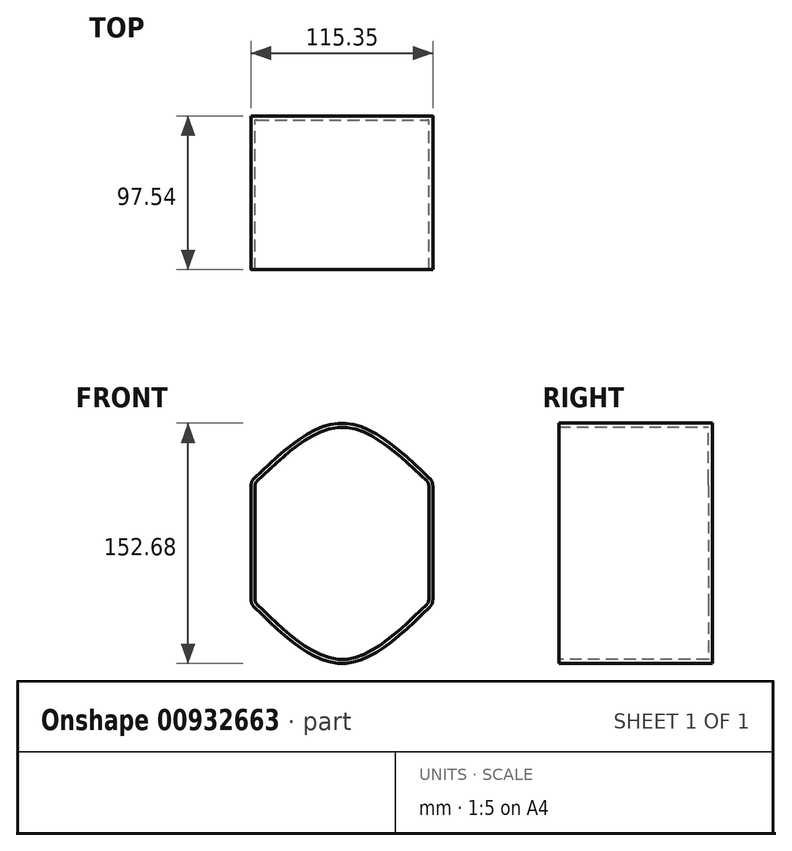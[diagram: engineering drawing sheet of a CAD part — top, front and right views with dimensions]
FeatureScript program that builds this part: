
annotation { "Feature Type Name" : "Feature", "Feature Type Description" : "" }
export const myFeature = defineFeature(function(context is Context, id is Id, definition is map)
    precondition{}
    {
        {
            var Q0;
            Q0=qCreatedBy(makeId("Front.planeOp"),FACE);
            var sketch = newSketch(context, id + "F0", { "sketchPlane" : qUnion([Q0])});
            skLineSegment(sketch, "E0.left", {"start": v(-56.92, 36.54) * mm, "end": v(-56.92, -36.1) * mm});
            skLineSegment(sketch, "E0.right", {"start": v(58.43, 36.54) * mm, "end": v(58.43, -36.1) * mm});
            skFitSpline(sketch, "E1", {"points": [v(-56.92, 39.25) * mm, v(0.75, 76.2) * mm, v(58.43, 39.25) * mm], "startDerivative": vector(115.35, 110.85) * mm, "endDerivative": vector(115.35, -110.85) * mm});
            skFitSpline(sketch, "E2", {"points": [v(-56.92, -38.77) * mm, v(0.75, -76.48) * mm, v(58.43, -38.77) * mm], "startDerivative": vector(115.35, -113.14) * mm, "endDerivative": vector(115.35, 113.14) * mm});
            skArc(sketch, "E3.filletArc", {"start": v(-54.97, 41.12) * mm, "mid": v(-56.41, 39.03) * mm, "end": v(-56.92, 36.54) * mm});
            skArc(sketch, "E4.filletArc", {"start": v(-56.92, -36.1) * mm, "mid": v(-56.43, -38.56) * mm, "end": v(-55.02, -40.63) * mm});
            skArc(sketch, "E5.filletArc", {"start": v(56.52, -40.63) * mm, "mid": v(57.93, -38.56) * mm, "end": v(58.43, -36.1) * mm});
            skArc(sketch, "E6.filletArc", {"start": v(58.43, 36.54) * mm, "mid": v(57.92, 39.03) * mm, "end": v(56.48, 41.12) * mm});
            skSolve(sketch);
        }
        {
            var Q0;
            Q0=makeQuery(id+"F0.imprint","IMPRINT",FACE,{"disambiguationData":[TD([[makeQuery(id+"F0.imprint","IMPRINT",EDGE,{"derivedFrom":sQuery(id+"F0.wireOp",EDGE,"E0.left")}),1.0]])]});
            extrude(context, id + "F1", {"entities" : qUnion([Q0]), "depth" : 97.54 * mm, "offsetDistance" : 25.4 * mm});
        }
        {
            var Q0;
            Q0=makeQuery(id+"F1.opExtrude","CAP_FACE",FACE,{"disambiguationData":[OSD([sQuery(id+"F0.wireOp",EDGE,"E0.left"),sQuery(id+"F0.wireOp",EDGE,"E0.right"),sQuery(id+"F0.wireOp",EDGE,"E1"),sQuery(id+"F0.wireOp",EDGE,"E2"),sQuery(id+"F0.wireOp",EDGE,"E3.filletArc"),sQuery(id+"F0.wireOp",EDGE,"E4.filletArc"),sQuery(id+"F0.wireOp",EDGE,"E5.filletArc"),sQuery(id+"F0.wireOp",EDGE,"E6.filletArc")])],"isStart":false});
            shell(context, id + "F2", {"entities" : qUnion([Q0]), "thickness" : 2.54 * mm});
        }
    });
